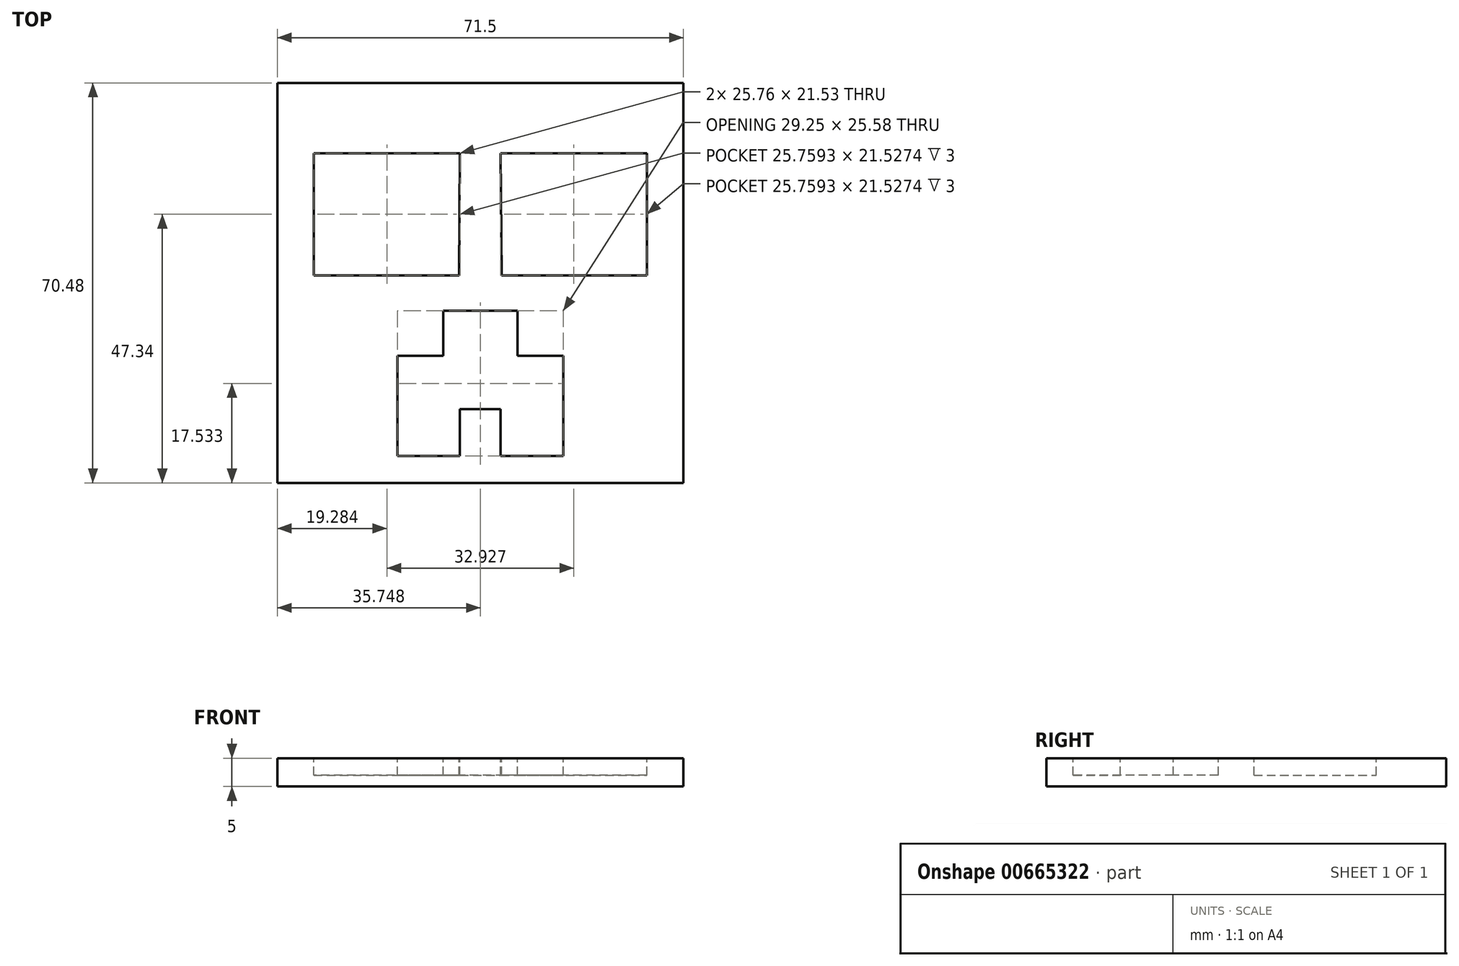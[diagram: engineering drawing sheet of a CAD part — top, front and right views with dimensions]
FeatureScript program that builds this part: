
annotation { "Feature Type Name" : "Feature", "Feature Type Description" : "" }
export const myFeature = defineFeature(function(context is Context, id is Id, definition is map)
    precondition{}
    {
        {
            var Q0;
            Q0=qCreatedBy(makeId("Top.planeOp"),FACE);
            var sketch = newSketch(context, id + "F0", { "sketchPlane" : qUnion([Q0])});
            skLineSegment(sketch, "E0", {"start": v(-37.04, -46.42) * mm, "end": v(34.46, -46.42) * mm});
            skLineSegment(sketch, "E1", {"start": v(34.46, -46.42) * mm, "end": v(34.46, 24.06) * mm});
            skLineSegment(sketch, "E2", {"start": v(34.46, 24.06) * mm, "end": v(-37.04, 24.06) * mm});
            skLineSegment(sketch, "E3", {"start": v(-37.04, 24.06) * mm, "end": v(-37.04, -46.42) * mm});
            skSolve(sketch);
        }
        {
            var Q0;
            Q0=makeQuery(id+"F0.imprint","IMPRINT",FACE,{"disambiguationData":[TD([[makeQuery(id+"F0.imprint","IMPRINT",EDGE,{"derivedFrom":sQuery(id+"F0.wireOp",EDGE,"E0")}),1.0]])]});
            extrude(context, id + "F1", {"entities" : qUnion([Q0]), "depth" : 5 * mm, "offsetDistance" : 25 * mm});
        }
        {
            var Q0;
            Q0=makeQuery(id+"F1.opExtrude","CAP_FACE",FACE,{"disambiguationData":[OSD([sQuery(id+"F0.wireOp",EDGE,"E0"),sQuery(id+"F0.wireOp",EDGE,"E1"),sQuery(id+"F0.wireOp",EDGE,"E2"),sQuery(id+"F0.wireOp",EDGE,"E3")])],"isStart":false});
            var sketch = newSketch(context, id + "F2", { "sketchPlane" : qUnion([Q0])});
            skLineSegment(sketch, "E4", {"start": v(-1.3, 24.06) * mm, "end": v(-1.3, -46.42) * mm});
            skLineSegment(sketch, "E5", {"start": v(-4.88, 11.68) * mm, "end": v(-30.64, 11.68) * mm});
            skLineSegment(sketch, "E6", {"start": v(-30.64, 11.68) * mm, "end": v(-30.64, -9.84) * mm});
            skLineSegment(sketch, "E7", {"start": v(-30.64, -9.84) * mm, "end": v(-5.06, -9.84) * mm});
            skLineSegment(sketch, "E8", {"start": v(-5.06, -9.84) * mm, "end": v(-4.88, 11.68) * mm});
            skLineSegment(sketch, "E9", {"start": v(-1.3, -16.1) * mm, "end": v(-7.82, -16.1) * mm});
            skLineSegment(sketch, "E10", {"start": v(-7.82, -16.1) * mm, "end": v(-7.82, -24.01) * mm});
            skLineSegment(sketch, "E11", {"start": v(-7.82, -24.01) * mm, "end": v(-15.92, -24.01) * mm});
            skLineSegment(sketch, "E12", {"start": v(-15.92, -24.01) * mm, "end": v(-15.92, -41.67) * mm});
            skLineSegment(sketch, "E13", {"start": v(-15.92, -41.67) * mm, "end": v(-4.88, -41.67) * mm});
            skLineSegment(sketch, "E14", {"start": v(-4.88, -41.67) * mm, "end": v(-4.88, -33.4) * mm});
            skLineSegment(sketch, "E15", {"start": v(-4.88, -33.4) * mm, "end": v(-1.3, -33.4) * mm});
            skLineSegment(sketch, "E16", {"start": v(-1.3, -33.4) * mm, "end": v(-1.3, -16.1) * mm});
            skLineSegment(sketch, "E17.MirrorCS", {"start": v(2.3, 11.68) * mm, "end": v(28.05, 11.68) * mm});
            skLineSegment(sketch, "E18.MirrorCS", {"start": v(2.48, -9.84) * mm, "end": v(2.3, 11.68) * mm});
            skLineSegment(sketch, "E19.MirrorCS", {"start": v(28.05, -9.84) * mm, "end": v(2.48, -9.84) * mm});
            skLineSegment(sketch, "E20.MirrorCS", {"start": v(28.05, 11.68) * mm, "end": v(28.05, -9.84) * mm});
            skLineSegment(sketch, "E21.MirrorCS", {"start": v(-1.3, -16.1) * mm, "end": v(5.24, -16.1) * mm});
            skLineSegment(sketch, "E22.MirrorCS", {"start": v(5.24, -16.1) * mm, "end": v(5.24, -24.01) * mm});
            skLineSegment(sketch, "E23.MirrorCS", {"start": v(5.24, -24.01) * mm, "end": v(13.33, -24.01) * mm});
            skLineSegment(sketch, "E24.MirrorCS", {"start": v(13.33, -24.01) * mm, "end": v(13.33, -41.67) * mm});
            skLineSegment(sketch, "E25.MirrorCS", {"start": v(13.33, -41.67) * mm, "end": v(2.3, -41.67) * mm});
            skLineSegment(sketch, "E26.MirrorCS", {"start": v(2.3, -41.67) * mm, "end": v(2.3, -33.4) * mm});
            skLineSegment(sketch, "E27.MirrorCS", {"start": v(2.3, -33.4) * mm, "end": v(-1.3, -33.4) * mm});
            skSolve(sketch);
        }
        {
            var Q0;
            Q0 = qSketchRegion(id + "F2", true);
            extrude(context, id + "F3", {"entities" : qUnion([Q0]), "operationType" : NewBodyOperationType.REMOVE, "oppositeDirection" : true, "depth" : 3 * mm, "offsetDistance" : 25 * mm});
        }
    });
